# Revit family: Bath_Shower_Seat-Wall_Hung-Bobrick-B-5191
name_source: partatom
category: Specialty Equipment
revit_build: Autodesk Revit 2016 (Build: 20150714_1515(x64)
units: mm (PartAtom-declared; Revit-internal decimal feet)

## family parameters
Cut with Voids When Loaded = No
Host = Face
OmniClass Number = 23.40.20.00
OmniClass Title = General Furniture and Specialties
Part Type = Normal
Room Calculation Point = No
Round Connector Dimension = Use Diameter
Shared = Yes

## types (1)
- B-5191
    ADA Compliant = Yes
    ATS URL = http://www.atsspec.net
    Assembly Code = E1020810
    Default Elevation = 17"
    Description = Bobrick Solid Phenolic Folding Shower/Dressing Area Seat
    Height = 13 3/4"
    Installation Type = Wall Mounted
    Length = 15 13/16"
    Manufacturer = Bobrick
    Masterformat Number = 12 52 70
    Masterformat Title = Healthcare Seating
    Material = Phenolic-Bobrick-Matte-Ivory
    Model = B-5191
    Omniclass Table 23 Code = 23.40.20.00
    Omniclass Table 23 Title = General Furniture and Specialties
    Price = Prices may vary. Please consult Manufacturer Representative for most up-to-date price list.
    Product Documentation Link = https://www.bobrick.com
    Product Page URL = https://www.bobrick.com
    Safety Warning = SAFETY WARNING: Shower seats are no stronger than the anchors and walls to which they are attached and must be firmly secured in order to support the loads for which they are intended. Consult and comply with local building codes. To avoid potential injury, the building owner or maintenance personnel should remove the shower seat from service if the shower seat is not adequately secured to the wall. Unit shall support static loads of up to 500 lbs (227 kg) when properly installed and used. To avoid potential seat malfunction, DO NOT use seat if weight exceeds 500 lbs (227 kg).
    Specification = Folding shower seat shall have a frame constructed of type-304, satin-finish stainless steel that consists of 16-gauge (1.6mm), 1-1/4'' (30mm) square tubing and 18-gauge (1.2mm), 1'' (25mm) diameter seamless tubing. Seat shall be one‑piece, 5/16" (8mm) thick, solidly fused plastic laminate with matte-finish melamine surfaces, ivory-colored face sheets, and black phenolicresin core; secured to frame with stainless steel carriage bolts and acorn nuts. Shower seat shall be equipped with two 3'' (75mm) diameter mounting flanges constructed of type-304, 3/16'' (5mm) thick, satin-finish stainless steel; a guide bracket constructed of type-304, 16-gauge (1.6mm), satin-finish stainless steel; and a spring constructed of type-301, 24-gauge (0.6mm) stainless steel that is spot-welded to a baseplate of type-304, heavy-gauge stainless steel. Seat shall be able to lock in upright position when not in use. Shower seat shall comply with accessible design guidelines (including ADAAG in the U.S.A.). Folding Shower Seat shall be Model B-5192 of Bobrick Washroom Equipment, Inc., Clifton Park, New York; Jackson, Tennessee; Los Angeles, California; Bobrick Washroom Equipment Company, Scarborough, Ontario; Bobrick Washroom Equipment Pty. Ltd., Australia; and Bobrick Washroom Equipment Limited, United Kingdom.
    URL = http://www.bobrick.com
    Width = 22"

## geometry (parser evidence)
native form markers: Sweep x2
no freeform markers — native parametric forms only
